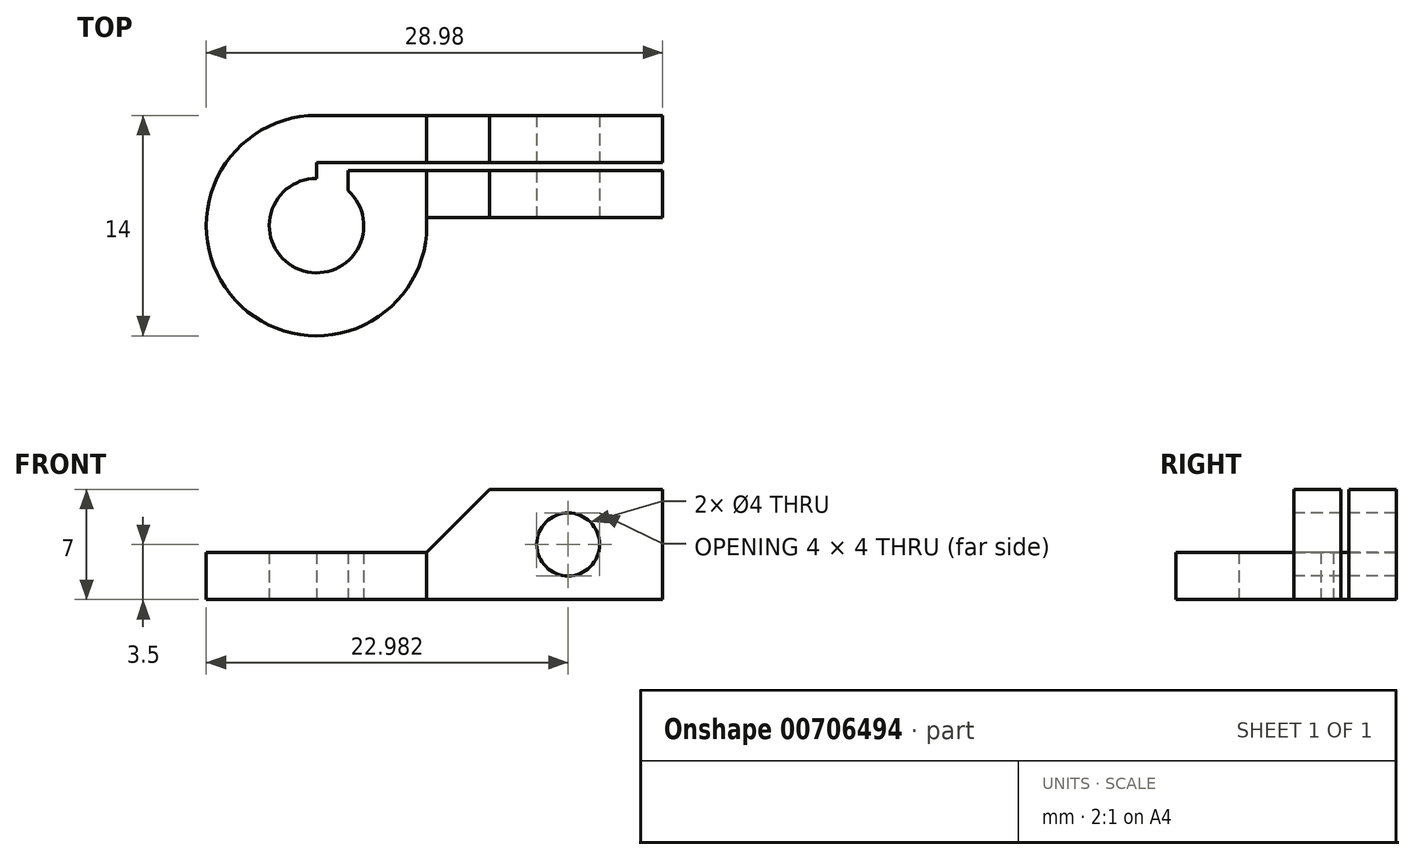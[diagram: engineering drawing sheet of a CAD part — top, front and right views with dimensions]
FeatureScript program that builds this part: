
annotation { "Feature Type Name" : "Feature", "Feature Type Description" : "" }
export const myFeature = defineFeature(function(context is Context, id is Id, definition is map)
    precondition{}
    {
        {
            var Q0;
            Q0=qCreatedBy(makeId("Top.planeOp"),FACE);
            var sketch = newSketch(context, id + "F0", { "sketchPlane" : qUnion([Q0])});
            skArc(sketch, "E0", {"start": v(0, 3) * mm, "mid": v(-1.07, -2.8) * mm, "end": v(2, 2.24) * mm});
            skArc(sketch, "E1", {"start": v(0, 7) * mm, "mid": v(-4.77, -5.12) * mm, "end": v(6.98, 0.5) * mm});
            skLineSegment(sketch, "E2", {"start": v(0, 7) * mm, "end": v(21.98, 7) * mm});
            skLineSegment(sketch, "E3", {"start": v(21.98, 7) * mm, "end": v(21.98, 4) * mm});
            skLineSegment(sketch, "E4", {"start": v(2, 3.5) * mm, "end": v(21.98, 3.5) * mm});
            skLineSegment(sketch, "E5", {"start": v(21.98, 3.5) * mm, "end": v(21.98, 0.5) * mm});
            skLineSegment(sketch, "E6", {"start": v(21.98, 0.5) * mm, "end": v(6.98, 0.5) * mm});
            skLineSegment(sketch, "E7", {"start": v(21.98, 4) * mm, "end": v(0, 4) * mm});
            skLineSegment(sketch, "E8", {"start": v(0, 4) * mm, "end": v(0, 3) * mm});
            skLineSegment(sketch, "E9", {"start": v(2, 3.5) * mm, "end": v(2, 2.24) * mm});
            skSolve(sketch);
        }
        {
            var Q0;
            Q0=makeQuery(id+"F0.imprint","IMPRINT",FACE,{"disambiguationData":[TD([[makeQuery(id+"F0.imprint","IMPRINT",EDGE,{"derivedFrom":sQuery(id+"F0.wireOp",EDGE,"E0")}),-1.0]])]});
            extrude(context, id + "F1", {"entities" : qUnion([Q0]), "depth" : 3 * mm, "offsetDistance" : 25 * mm});
        }
        {
            var Q0;
            Q0=makeQuery(id+"F1.opExtrude","CAP_FACE",FACE,{"disambiguationData":[OSD([sQuery(id+"F0.wireOp",EDGE,"E0"),sQuery(id+"F0.wireOp",EDGE,"E1"),sQuery(id+"F0.wireOp",EDGE,"E2"),sQuery(id+"F0.wireOp",EDGE,"E3"),sQuery(id+"F0.wireOp",EDGE,"E4"),sQuery(id+"F0.wireOp",EDGE,"E5"),sQuery(id+"F0.wireOp",EDGE,"E6"),sQuery(id+"F0.wireOp",EDGE,"E7")])],"isStart":false});
            var sketch = newSketch(context, id + "F2", { "sketchPlane" : qUnion([Q0])});
            skLineSegment(sketch, "E10.bottom", {"start": v(6.98, 0.5) * mm, "end": v(21.98, 0.5) * mm});
            skLineSegment(sketch, "E10.top", {"start": v(6.98, 3.5) * mm, "end": v(21.98, 3.5) * mm});
            skLineSegment(sketch, "E10.left", {"start": v(6.98, 0.5) * mm, "end": v(6.98, 3.5) * mm});
            skLineSegment(sketch, "E10.right", {"start": v(21.98, 0.5) * mm, "end": v(21.98, 3.5) * mm});
            skLineSegment(sketch, "E11.bottom", {"start": v(6.98, 4) * mm, "end": v(21.98, 4) * mm});
            skLineSegment(sketch, "E11.top", {"start": v(6.98, 7) * mm, "end": v(21.98, 7) * mm});
            skLineSegment(sketch, "E11.left", {"start": v(6.98, 4) * mm, "end": v(6.98, 7) * mm});
            skLineSegment(sketch, "E11.right", {"start": v(21.98, 4) * mm, "end": v(21.98, 7) * mm});
            skSolve(sketch);
        }
        {
            var Q0;
            Q0=makeQuery(id+"F2.imprint","IMPRINT",FACE,{"disambiguationData":[TD([[makeQuery(id+"F2.imprint","IMPRINT",EDGE,{"derivedFrom":sQuery(id+"F2.wireOp",EDGE,"E11.bottom")}),-1.0]])]});
            var Q1;
            Q1=makeQuery(id+"F2.imprint","IMPRINT",FACE,{"disambiguationData":[TD([[makeQuery(id+"F2.imprint","IMPRINT",EDGE,{"derivedFrom":sQuery(id+"F2.wireOp",EDGE,"E10.bottom")}),-1.0]])]});
            extrude(context, id + "F3", {"entities" : qUnion([Q0, Q1]), "operationType" : NewBodyOperationType.ADD, "depth" : 4 * mm, "offsetDistance" : 25 * mm});
        }
        {
            var Q0;
            Q0=makeQuery(id+"F3.boolean.opBoolean","MERGE",FACE,{"derivedFrom":[makeQuery(id+"F1.opExtrude","SWEPT_FACE",FACE,{"disambiguationData":[OSD([sQuery(id+"F0.wireOp",EDGE,"E6")])]}),makeQuery(id+"F3.opExtrude","SWEPT_FACE",FACE,{"disambiguationData":[OSD([sQuery(id+"F2.wireOp",EDGE,"E10.bottom")])]})]});
            var sketch = newSketch(context, id + "F4", { "sketchPlane" : qUnion([Q0])});
            skLineSegment(sketch, "E12", {"start": v(6.98, 3) * mm, "end": v(10.98, 7) * mm});
            skLineSegment(sketch, "E13", {"start": v(10.98, 7) * mm, "end": v(6.98, 7) * mm});
            skLineSegment(sketch, "E14", {"start": v(6.98, 7) * mm, "end": v(6.98, 3) * mm});
            skSolve(sketch);
        }
        {
            var Q0;
            Q0=makeQuery(id+"F4.imprint","IMPRINT",FACE,{"disambiguationData":[TD([[makeQuery(id+"F4.imprint","IMPRINT",EDGE,{"derivedFrom":sQuery(id+"F4.wireOp",EDGE,"E12")}),1.0]])]});
            extrude(context, id + "F5", {"entities" : qUnion([Q0]), "operationType" : NewBodyOperationType.REMOVE, "endBound" : BoundingType.THROUGH_ALL, "oppositeDirection" : true, "depth" : 25 * mm, "offsetDistance" : 25 * mm});
        }
        {
            var Q0;
            Q0=makeQuery(id+"F3.boolean.opBoolean","MERGE",FACE,{"derivedFrom":[makeQuery(id+"F1.opExtrude","SWEPT_FACE",FACE,{"disambiguationData":[OSD([sQuery(id+"F0.wireOp",EDGE,"E6")])]}),makeQuery(id+"F3.opExtrude","SWEPT_FACE",FACE,{"disambiguationData":[OSD([sQuery(id+"F2.wireOp",EDGE,"E10.bottom")])]})]});
            var sketch = newSketch(context, id + "F6", { "sketchPlane" : qUnion([Q0])});
            skCircle(sketch, "E15", {"center": v(15.98, 3.5) * mm, "radius": 2 * mm});
            skPoint(sketch, "E15.centerSnap0", {"position": v(21.98, 3.5) * mm});
            skSolve(sketch);
        }
        {
            var Q0;
            Q0=makeQuery(id+"F6.imprint","IMPRINT",FACE,{"disambiguationData":[TD([[makeQuery(id+"F6.imprint","IMPRINT",EDGE,{"derivedFrom":sQuery(id+"F6.wireOp",EDGE,"E15")}),1.0]])]});
            extrude(context, id + "F7", {"entities" : qUnion([Q0]), "operationType" : NewBodyOperationType.REMOVE, "endBound" : BoundingType.THROUGH_ALL, "oppositeDirection" : true, "depth" : 25 * mm, "offsetDistance" : 25 * mm});
        }
    });
